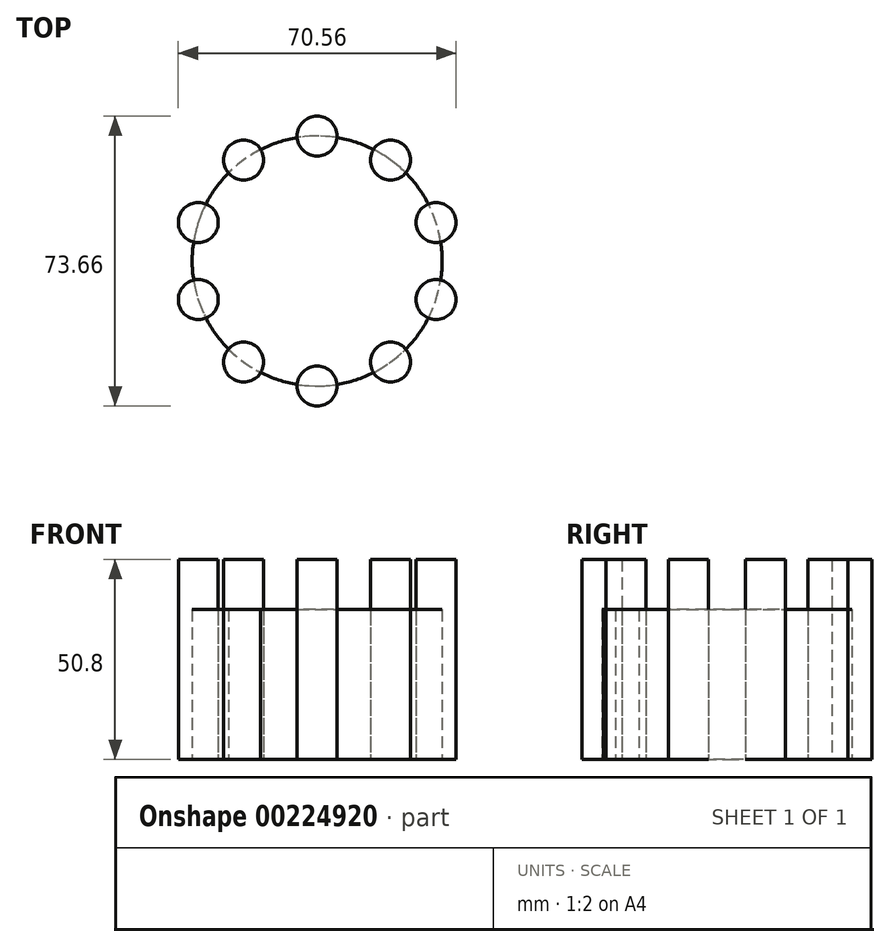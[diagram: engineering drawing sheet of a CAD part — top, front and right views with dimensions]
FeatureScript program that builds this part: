
annotation { "Feature Type Name" : "Feature", "Feature Type Description" : "" }
export const myFeature = defineFeature(function(context is Context, id is Id, definition is map)
    precondition{}
    {
        {
            var Q0;
            Q0=qCreatedBy(makeId("Top.planeOp"),FACE);
            var sketch = newSketch(context, id + "F0", { "sketchPlane" : qUnion([Q0])});
            skCircle(sketch, "E0", {"center": v(0, 0) * mm, "radius": 31.75 * mm});
            skSolve(sketch);
        }
        {
            var Q0;
            Q0=qSketchRegion(id+"F0",true);
            extrude(context, id + "F1", {"entities" : qUnion([Q0]), "depth" : 38.1 * mm});
        }
        {
            var Q0;
            Q0=qCreatedBy(makeId("Top.planeOp"),FACE);
            var sketch = newSketch(context, id + "F2", { "sketchPlane" : qUnion([Q0])});
            skCircle(sketch, "E1", {"center": v(0, 31.75) * mm, "radius": 5.08 * mm});
            skCircle(sketch, "E2.1.0", {"center": v(-18.66, 25.69) * mm, "radius": 5.08 * mm});
            skCircle(sketch, "E2.2.0", {"center": v(-30.2, 9.81) * mm, "radius": 5.08 * mm});
            skCircle(sketch, "E2.3.0", {"center": v(-30.2, -9.81) * mm, "radius": 5.08 * mm});
            skCircle(sketch, "E2.4.0", {"center": v(-18.66, -25.69) * mm, "radius": 5.08 * mm});
            skCircle(sketch, "E2.5.0", {"center": v(0, -31.75) * mm, "radius": 5.08 * mm});
            skCircle(sketch, "E2.6.0", {"center": v(18.66, -25.69) * mm, "radius": 5.08 * mm});
            skCircle(sketch, "E2.7.0", {"center": v(30.2, -9.81) * mm, "radius": 5.08 * mm});
            skCircle(sketch, "E2.8.0", {"center": v(30.2, 9.81) * mm, "radius": 5.08 * mm});
            skCircle(sketch, "E2.9.0", {"center": v(18.66, 25.69) * mm, "radius": 5.08 * mm});
            skPoint(sketch, "E2.center", {"position": v(0, 0) * mm});
            skSolve(sketch);
        }
        {
            var Q0;
            Q0=qSketchRegion(id+"F2",true);
            extrude(context, id + "F3", {"entities" : qUnion([Q0]), "depth" : 50.8 * mm});
        }
        {
            var Q0;
            Q0=makeQuery(id+"F1.opExtrude","SWEPT_BODY",BODY,{"disambiguationData":[OSD([sQuery(id+"F0.wireOp",EDGE,"E0")])]});
            var Q1;
            Q1=makeQuery(id+"F3.opExtrude","SWEPT_BODY",BODY,{"disambiguationData":[OSD([sQuery(id+"F2.wireOp",EDGE,"E2.5.0")])]});
            booleanBodies(context, id + "F4", {"operationType" : BooleanOperationType.INTERSECTION, "tools" : qUnion([Q0, Q1]), "keepTools" : true});
        }
        {
            var Q0;
            Q0=makeQuery(id+"F1.opExtrude","SWEPT_BODY",BODY,{"disambiguationData":[OSD([sQuery(id+"F0.wireOp",EDGE,"E0")])]});
            var Q1;
            Q1=makeQuery(id+"F3.opExtrude","SWEPT_BODY",BODY,{"disambiguationData":[OSD([sQuery(id+"F2.wireOp",EDGE,"E2.4.0")])]});
            booleanBodies(context, id + "F5", {"operationType" : BooleanOperationType.INTERSECTION, "tools" : qUnion([Q0, Q1]), "keepTools" : true});
        }
        {
            var Q0;
            Q0=makeQuery(id+"F3.opExtrude","SWEPT_BODY",BODY,{"disambiguationData":[OSD([sQuery(id+"F2.wireOp",EDGE,"E2.4.0")])]});
            var Q1;
            Q1=makeQuery(id+"F1.opExtrude","SWEPT_BODY",BODY,{"disambiguationData":[OSD([sQuery(id+"F0.wireOp",EDGE,"E0")])]});
            booleanBodies(context, id + "F6", {"operationType" : BooleanOperationType.INTERSECTION, "tools" : qUnion([Q0, Q1]), "keepTools" : true});
        }
    });
